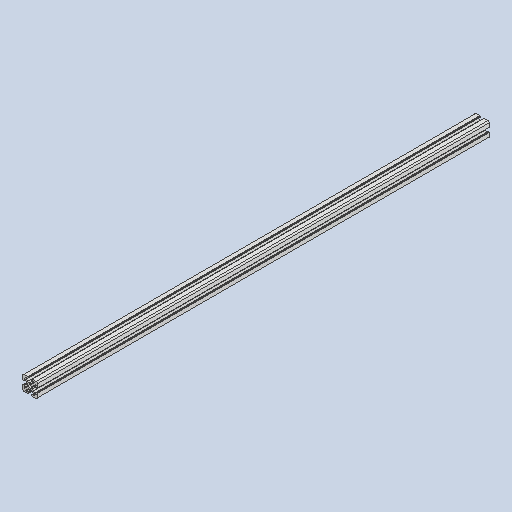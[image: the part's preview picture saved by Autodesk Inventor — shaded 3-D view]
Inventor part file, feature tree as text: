
AUTODESK INVENTOR PART (.ipt)
format: ipt  version: 2023 (Build 270158000, 158)  size: 325,632 bytes
history: mixed  units: in
note: dims shown in document units (in); Inventor stores cm internally (conversion verified against a paired STEP export)
features: mirror x1, imported_body x1
ambient origin geometry x8: Origin, YZ Plane, XZ Plane, XY Plane, X Axis, Y Axis, Z Axis, Center Point
bodies: Solid1 (imported_parasolid)
feature tree (2):
  mirror  "Mirror2"
  imported_body  NMx_Import_Brep_tag  [imported B-rep: ~75 faces, bbox_mm=[20.0, 20.0, 609.6]]
